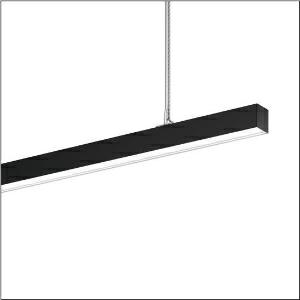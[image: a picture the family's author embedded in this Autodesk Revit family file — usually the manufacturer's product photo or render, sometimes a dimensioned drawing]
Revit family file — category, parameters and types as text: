
# Revit family: silica_r__21_51mx30db45bb_77a6
name_source: partatom
category: Lighting Fixtures
units: mm (PartAtom-declared; Revit-internal decimal feet)

## family parameters
Cut with Voids When Loaded = No
Host = Face
Light Source = No
Part Type = Normal
Room Calculation Point = No
Round Connector Dimension = Use Diameter
Shared = No

## types (1)
- --- (1 x LED, 5260 lm, 32 W, 4000K)
    Apparent Load = 32 VA
    CIE Flux Codes = 47 79 96 57 100
    Color Rendering = 80
    Color Temperature = 4000K
    Default Elevation = 1800 mm
    Description = Silica® 21, office luminaire, primary optical cover: cover, of PMMA, opal, light emission: direct/indirect distribution, primary light characteristic: symmetric, installation type: suspended mounting, LED, rated luminous flux: 5.260lm, luminous efficacy: 164lm/W, light colour: 840, colour temperature: 4000K, with terminal, 3+2-pole, max. 2.5mm², mains connection: 220..240V, AC, 50/60Hz, rated input power: 32W, luminaire housing, of aluminium, jet black (RAL 9005), length: 1.504mm, width: 53mm, height: 53mm, protection rating (complete): IP20, insulation class (complete): insulation class I (protective earthing), certification: CE, permissible operating ambient temperature: 0..+35°C, standard: EN 50419, packaging unit: 1 piece
    Height = 53 mm
    Lamp = 1 x LED
    Lamp Light Flux = 5260 lm
    Lamp Power = 32 W
    Lamp count = 1
    Length = 1504 mm
    Luminous efficacy = 164 lm/W
    Manufacturer = Siteco
    ModVariant = No
    Model = 51MX30DB45BB
    Mounting Place = Ceiling
    Mounting Type = Pendant
    Number of Poles = 1
    OnlyDefault = Yes
    Power Factor = 1
    Product Name = Silica® 21
    Product group = office luminaire | ceiling pendant
    ProductGroupID = 902
    Protection Class = Protection class I
    Protection Degree = IP 20
    RLX_Detail_Level = 1
    RLX_Emergency_Light_Flux = 0 lm
    RLX_Emergency_Type = 0
    RLX_Emergency_Type_DB = No
    RlxData = <blob elided: 25949 chars, md5=2e0c5995>
    Socket = socket
    Standby Power = 0 W
    System Light Flux = 5260 lm
    System Power = 32 W
    Type Comments = factory setting: luminous flux: 100 % | dim-lin: 254 | 218 mA
    Type Image = l_1313646.jpg
    URL = http://relux.com
    VarID = @adj_065217
    Voltage = 0 V
    Weight = 0.00 kg
    Width = 53 mm

## geometry (parser evidence)
native form markers: Blend x4, Sweep x13
no freeform markers — native parametric forms only
